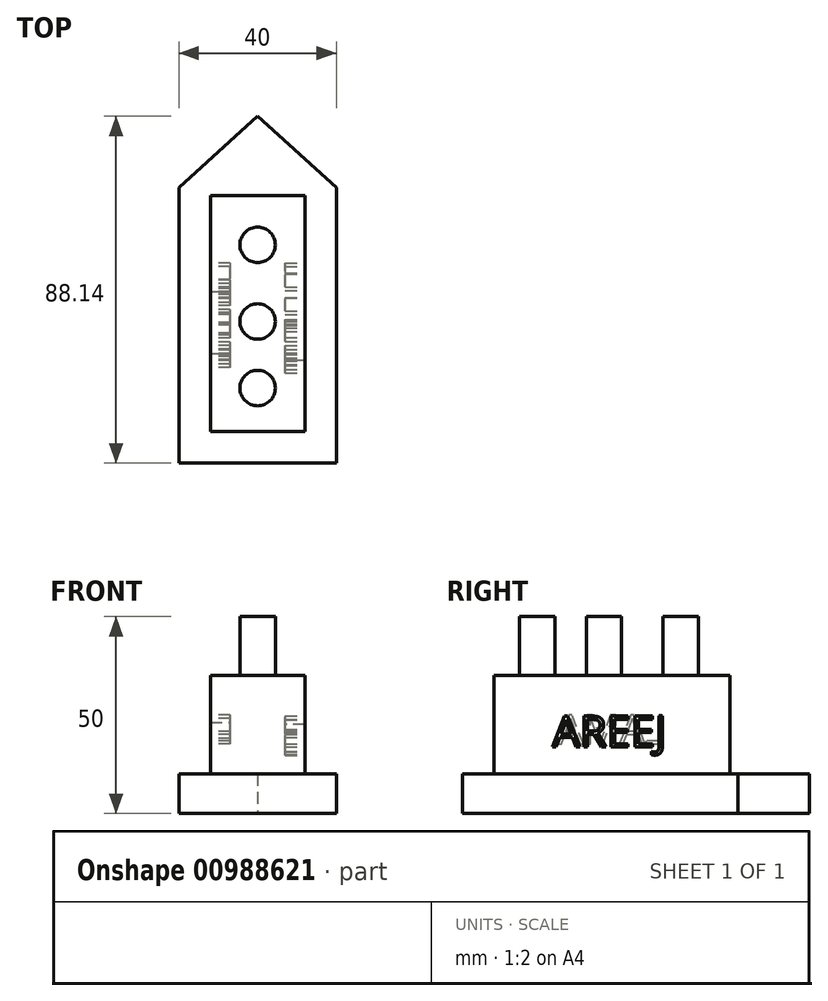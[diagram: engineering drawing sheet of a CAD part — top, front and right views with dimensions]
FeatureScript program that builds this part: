
annotation { "Feature Type Name" : "Feature", "Feature Type Description" : "" }
export const myFeature = defineFeature(function(context is Context, id is Id, definition is map)
    precondition{}
    {
        {
            var Q0;
            Q0=qCreatedBy(makeId("Top.planeOp"),FACE);
            var sketch = newSketch(context, id + "F0", { "sketchPlane" : qUnion([Q0])});
            skLineSegment(sketch, "E0", {"start": v(20, -40.57) * mm, "end": v(-20, -40.57) * mm});
            skLineSegment(sketch, "E1", {"start": v(20, -40.57) * mm, "end": v(20, 29.43) * mm});
            skLineSegment(sketch, "E2", {"start": v(-20, -40.57) * mm, "end": v(-20, 29.43) * mm});
            skLineSegment(sketch, "E3", {"start": v(20, 29.43) * mm, "end": v(0, 47.57) * mm});
            skLineSegment(sketch, "E4", {"start": v(-20, 29.43) * mm, "end": v(0, 47.57) * mm});
            skSolve(sketch);
        }
        {
            var Q0;
            Q0=makeQuery(id+"F0.imprint","IMPRINT",FACE,{"disambiguationData":[TD([[makeQuery(id+"F0.imprint","IMPRINT",EDGE,{"derivedFrom":sQuery(id+"F0.wireOp",EDGE,"E0")}),-1.0]])]});
            extrude(context, id + "F1", {"entities" : qUnion([Q0]), "depth" : 10 * mm, "offsetDistance" : 25 * mm});
        }
        {
            var Q0;
            Q0=makeQuery(id+"F1.opExtrude","CAP_FACE",FACE,{"disambiguationData":[OSD([sQuery(id+"F0.wireOp",EDGE,"E0"),sQuery(id+"F0.wireOp",EDGE,"E1"),sQuery(id+"F0.wireOp",EDGE,"E2"),sQuery(id+"F0.wireOp",EDGE,"E3"),sQuery(id+"F0.wireOp",EDGE,"E4")])],"isStart":false});
            var sketch = newSketch(context, id + "F2", { "sketchPlane" : qUnion([Q0])});
            skLineSegment(sketch, "E5", {"start": v(-12, 27.43) * mm, "end": v(-12, -32.57) * mm});
            skLineSegment(sketch, "E6", {"start": v(-12, -32.57) * mm, "end": v(12, -32.57) * mm});
            skLineSegment(sketch, "E7", {"start": v(12, -32.57) * mm, "end": v(12, 27.43) * mm});
            skLineSegment(sketch, "E8", {"start": v(12, 27.43) * mm, "end": v(-12, 27.43) * mm});
            skSolve(sketch);
        }
        {
            var Q0;
            Q0 = qSketchRegion(id + "F2", true);
            extrude(context, id + "F3", {"entities" : qUnion([Q0]), "operationType" : NewBodyOperationType.ADD, "depth" : 25 * mm, "offsetDistance" : 25 * mm});
        }
        {
            var Q0;
            Q0=makeQuery(id+"F3.opExtrude","CAP_FACE",FACE,{"disambiguationData":[OSD([sQuery(id+"F2.wireOp",EDGE,"E5"),sQuery(id+"F2.wireOp",EDGE,"E6"),sQuery(id+"F2.wireOp",EDGE,"E7"),sQuery(id+"F2.wireOp",EDGE,"E8")])],"isStart":false});
            var sketch = newSketch(context, id + "F4", { "sketchPlane" : qUnion([Q0])});
            skCircle(sketch, "E9", {"center": v(0, 14.87) * mm, "radius": 4.5 * mm});
            skCircle(sketch, "E10", {"center": v(0, -4.6) * mm, "radius": 4.5 * mm});
            skCircle(sketch, "E11", {"center": v(0, -21.51) * mm, "radius": 4.5 * mm});
            skSolve(sketch);
        }
        {
            var Q0;
            Q0 = qSketchRegion(id + "F4", true);
            extrude(context, id + "F5", {"entities" : qUnion([Q0]), "operationType" : NewBodyOperationType.ADD, "depth" : 15 * mm, "offsetDistance" : 25 * mm});
        }
        {
            var Q0;
            Q0=makeQuery(id+"F3.opExtrude","SWEPT_FACE",FACE,{"disambiguationData":[OSD([sQuery(id+"F2.wireOp",EDGE,"E5")])]});
            var sketch = newSketch(context, id + "F6", { "sketchPlane" : qUnion([Q0])});
            skText(sketch, "E12", { "text": "LAMA", "fontName": "OpenSans-Regular.ttf"});
            const initialGuessF6  = {"E12": [-0.01119, 0.0177, 1, 0, 0.00737]};
            skSetInitialGuess(sketch, initialGuessF6);
            skSolve(sketch);
        }
        {
            var Q0;
            Q0=makeQuery(id+"F3.opExtrude","SWEPT_FACE",FACE,{"disambiguationData":[OSD([sQuery(id+"F2.wireOp",EDGE,"E7")])]});
            var sketch = newSketch(context, id + "F7", { "sketchPlane" : qUnion([Q0])});
            skText(sketch, "E13", { "text": "AREEJ", "fontName": "OpenSans-Regular.ttf"});
            const initialGuessF7  = {"E13": [-0.0177, 0.01685, 1, 0, 0.00793]};
            skSetInitialGuess(sketch, initialGuessF7);
            skSolve(sketch);
        }
        {
            var Q0;
            Q0 = qSketchRegion(id + "F7", true);
            extrude(context, id + "F8", {"entities" : qUnion([Q0]), "operationType" : NewBodyOperationType.REMOVE, "oppositeDirection" : true, "depth" : 5 * mm, "offsetDistance" : 25 * mm});
        }
        {
            var Q0;
            Q0 = qSketchRegion(id + "F6", true);
            extrude(context, id + "F9", {"entities" : qUnion([Q0]), "operationType" : NewBodyOperationType.REMOVE, "oppositeDirection" : true, "depth" : 5 * mm, "offsetDistance" : 25 * mm});
        }
    });
